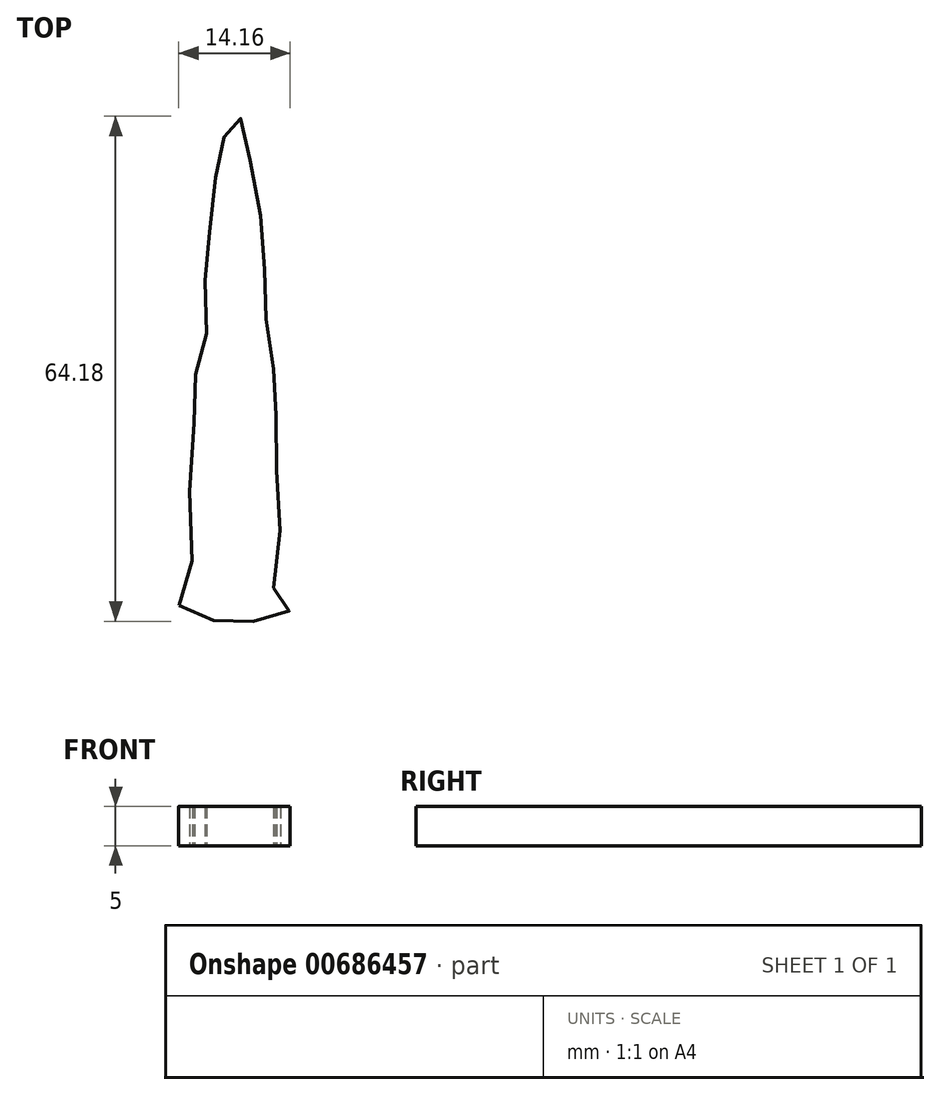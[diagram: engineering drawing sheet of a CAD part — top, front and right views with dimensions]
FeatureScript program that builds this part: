
annotation { "Feature Type Name" : "Feature", "Feature Type Description" : "" }
export const myFeature = defineFeature(function(context is Context, id is Id, definition is map)
    precondition{}
    {
        {
            var Q0;
            Q0=qCreatedBy(makeId("Top.planeOp"),FACE);
            var sketch = newSketch(context, id + "F0", { "sketchPlane" : qUnion([Q0])});
            skFitSpline(sketch, "E0", {"points": [v(-48.55, 4.1) * mm, v(-46.01, 2.54) * mm, v(-42.3, 2.15) * mm, v(-38.59, 2.15) * mm, v(-35.07, 2.93) * mm, v(-34.49, 4.1) * mm, v(-36.24, 5.47) * mm, v(-35.85, 11.53) * mm, v(-36.05, 19.93) * mm, v(-36.24, 27.16) * mm, v(-36.24, 32.63) * mm, v(-37.22, 37.12) * mm, v(-37.61, 44.16) * mm, v(-37.8, 48.46) * mm, v(-38.59, 56.47) * mm, v(-39.96, 62.52) * mm, v(-40.74, 66.04) * mm, v(-41.32, 66.24) * mm, v(-42.7, 64.09) * mm, v(-43.67, 60.57) * mm, v(-44.25, 55.3) * mm, v(-45.04, 48.06) * mm, v(-45.23, 43.77) * mm, v(-45.23, 36.93) * mm, v(-46.4, 33.6) * mm, v(-46.6, 28.72) * mm, v(-47.19, 18.56) * mm, v(-47.19, 8.2) * mm, v(-48.55, 4.1) * mm]});
            skSolve(sketch);
        }
        {
            var Q0;
            Q0 = qSketchRegion(id + "F0", true);
            extrude(context, id + "F1", {"entities" : qUnion([Q0]), "depth" : 5 * mm, "offsetDistance" : 25.4 * mm});
        }
    });
